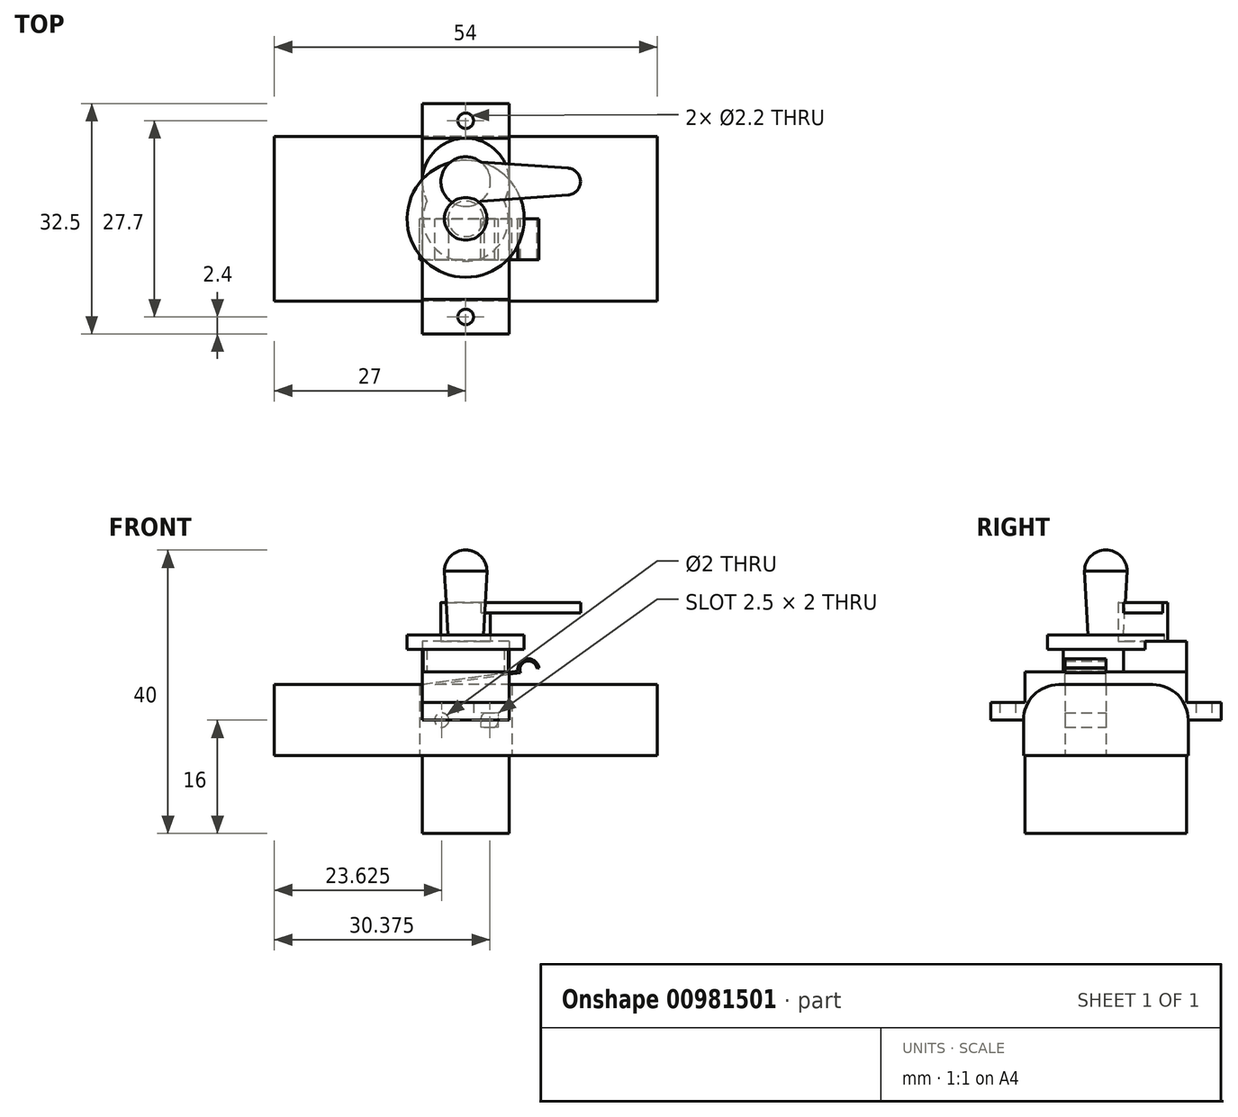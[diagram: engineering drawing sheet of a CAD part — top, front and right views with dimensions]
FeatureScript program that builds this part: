
annotation { "Feature Type Name" : "Feature", "Feature Type Description" : "" }
export const myFeature = defineFeature(function(context is Context, id is Id, definition is map)
    precondition{}
    {
        {
            var Q0;
            Q0=qCreatedBy(makeId("Right.planeOp"),FACE);
            var sketch = newSketch(context, id + "F0", { "sketchPlane" : qUnion([Q0])});
            skLineSegment(sketch, "E0.bottom", {"start": v(6.62, 5) * mm, "end": v(-6.63, 5) * mm});
            skLineSegment(sketch, "E0.top", {"start": v(11.63, -5) * mm, "end": v(-11.62, -5) * mm});
            skLineSegment(sketch, "E0.left", {"start": v(11.62, 0) * mm, "end": v(11.63, -5) * mm});
            skLineSegment(sketch, "E0.right", {"start": v(-11.63, 0) * mm, "end": v(-11.62, -5) * mm});
            skPoint(sketch, "E0.middle", {"position": v(0, 0) * mm});
            skPoint(sketch, "E1.visualSharp", {"position": v(-11.63, 5) * mm});
            skArc(sketch, "E1.filletArc", {"start": v(-6.63, 5) * mm, "mid": v(-10.16, 3.54) * mm, "end": v(-11.63, 0) * mm});
            skPoint(sketch, "E2.visualSharp", {"position": v(11.62, 5) * mm});
            skArc(sketch, "E2.filletArc", {"start": v(11.62, 0) * mm, "mid": v(10.16, 3.54) * mm, "end": v(6.62, 5) * mm});
            skSolve(sketch);
        }
        {
            var Q0;
            Q0 = qSketchRegion(id + "F0", true);
            extrude(context, id + "F1", {"entities" : qUnion([Q0]), "endBound" : BoundingType.SYMMETRIC, "depth" : 54 * mm, "offsetDistance" : 25 * mm});
        }
        {
            var Q0;
            Q0=qCreatedBy(makeId("Front.planeOp"),FACE);
            var sketch = newSketch(context, id + "F2", { "sketchPlane" : qUnion([Q0])});
            skLineSegment(sketch, "E3", {"start": v(0, 0) * mm, "end": v(0, 24) * mm});
            skArc(sketch, "E4", {"start": v(0, 24) * mm, "mid": v(2.12, 23.12) * mm, "end": v(3, 21) * mm});
            skLineSegment(sketch, "E5", {"start": v(3, 21) * mm, "end": v(2.5, 12) * mm});
            skLineSegment(sketch, "E6", {"start": v(2.5, 12) * mm, "end": v(6, 12) * mm});
            skLineSegment(sketch, "E7", {"start": v(6, 12) * mm, "end": v(6, 0) * mm});
            skLineSegment(sketch, "E8", {"start": v(0, 0) * mm, "end": v(6, 0) * mm});
            skSolve(sketch);
        }
        {
            var Q0;
            Q0 = qSketchRegion(id + "F2", true);
            var Q1;
            Q1=sQuery(id+"F2.wireOp",EDGE,"E3");
            revolve(context, id + "F3", {"surfaceOperationType" : NewSurfaceOperationType.NEW, "entities" : qUnion([Q0]), "axis" : qUnion([Q1]), "revolveType" : RevolveType.FULL});
        }
        {
            var Q0;
            Q0=makeQuery(id+"F3.opRevolve","SWEPT_FACE",FACE,{"disambiguationData":[OSD([sQuery(id+"F2.wireOp",EDGE,"E8")])]});
            var sketch = newSketch(context, id + "F4", { "sketchPlane" : qUnion([Q0])});
            skLineSegment(sketch, "E9.bottom", {"start": v(-5.75, 6.5) * mm, "end": v(5.75, 6.5) * mm});
            skLineSegment(sketch, "E9.top", {"start": v(-5.75, -6.5) * mm, "end": v(5.75, -6.5) * mm});
            skLineSegment(sketch, "E9.left", {"start": v(-5.75, 6.5) * mm, "end": v(-5.75, -6.5) * mm});
            skLineSegment(sketch, "E9.right", {"start": v(5.75, 6.5) * mm, "end": v(5.75, -6.5) * mm});
            skPoint(sketch, "E9.middle", {"position": v(0, 0) * mm});
            skSolve(sketch);
        }
        {
            var Q0;
            Q0 = qSketchRegion(id + "F4", true);
            extrude(context, id + "F5", {"entities" : qUnion([Q0]), "operationType" : NewBodyOperationType.ADD, "depth" : 13 * mm, "offsetDistance" : 25 * mm});
        }
        {
            var Q0;
            Q0=makeQuery(id+"F3.opRevolve","SWEPT_FACE",FACE,{"disambiguationData":[OSD([sQuery(id+"F2.wireOp",EDGE,"E6")])]});
            var sketch = newSketch(context, id + "F6", { "sketchPlane" : qUnion([Q0])});
            skCircle(sketch, "E10.cCircle", {"center": v(0, 0) * mm, "radius": 8.26 * mm});
            skLineSegment(sketch, "E10.0", {"start": v(8.26, 0) * mm, "end": v(4.13, -7.15) * mm, "construction": true});
            skLineSegment(sketch, "E10.1", {"start": v(4.13, -7.15) * mm, "end": v(-4.13, -7.15) * mm, "construction": true});
            skLineSegment(sketch, "E10.2", {"start": v(-4.13, -7.15) * mm, "end": v(-8.26, 0) * mm, "construction": true});
            skLineSegment(sketch, "E10.3", {"start": v(-8.26, 0) * mm, "end": v(-4.13, 7.15) * mm, "construction": true});
            skLineSegment(sketch, "E10.4", {"start": v(-4.13, 7.15) * mm, "end": v(4.13, 7.15) * mm, "construction": true});
            skLineSegment(sketch, "E10.5", {"start": v(4.13, 7.15) * mm, "end": v(8.26, 0) * mm, "construction": true});
            skSolve(sketch);
        }
        {
            var Q0;
            Q0 = qSketchRegion(id + "F6", true);
            var Q1;
            Q1 = qConstructionFilter(qBodyType(qCreatedBy(id + "F6" ,EDGE), BodyType.WIRE), ConstructionObject.NO);
            extrude(context, id + "F7", {"entities" : qUnion([Q0]), "operationType" : NewBodyOperationType.ADD, "surfaceOperationType" : NewSurfaceOperationType.ADD, "surfaceEntities" : qUnion([Q1]), "oppositeDirection" : true, "depth" : 2 * mm, "offsetDistance" : 25 * mm});
        }
        {
            var Q0;
            Q0=qCreatedBy(makeId("Top.planeOp"),FACE);
            var sketch = newSketch(context, id + "F8", { "sketchPlane" : qUnion([Q0])});
            skLineSegment(sketch, "E11.bottom", {"start": v(6.13, -11.38) * mm, "end": v(-6.12, -11.38) * mm});
            skLineSegment(sketch, "E11.top", {"start": v(6.12, 11.38) * mm, "end": v(-6.13, 11.38) * mm});
            skLineSegment(sketch, "E11.left", {"start": v(6.13, -11.38) * mm, "end": v(6.12, 11.38) * mm});
            skLineSegment(sketch, "E11.right", {"start": v(-6.12, -11.38) * mm, "end": v(-6.13, 11.37) * mm});
            skPoint(sketch, "E11.middle", {"position": v(0, 0) * mm});
            skSolve(sketch);
        }
        {
            var Q0;
            Q0 = qSketchRegion(id + "F8", true);
            extrude(context, id + "F9", {"entities" : qUnion([Q0]), "oppositeDirection" : true, "depth" : 16 * mm, "offsetDistance" : 25 * mm});
        }
        {
            var Q0;
            Q0=makeQuery(id+"F9.opExtrude","CAP_FACE",FACE,{"disambiguationData":[OSD([sQuery(id+"F8.wireOp",EDGE,"E11.bottom"),sQuery(id+"F8.wireOp",EDGE,"E11.top"),sQuery(id+"F8.wireOp",EDGE,"E11.left"),sQuery(id+"F8.wireOp",EDGE,"E11.right")])],"isStart":true});
            var sketch = newSketch(context, id + "F10", { "sketchPlane" : qUnion([Q0])});
            skLineSegment(sketch, "E12.bottom", {"start": v(6.13, -16.25) * mm, "end": v(-6.13, -16.25) * mm});
            skLineSegment(sketch, "E12.top", {"start": v(6.13, 16.25) * mm, "end": v(-6.13, 16.25) * mm});
            skLineSegment(sketch, "E12.left", {"start": v(6.13, -16.25) * mm, "end": v(6.13, 16.25) * mm});
            skLineSegment(sketch, "E12.right", {"start": v(-6.13, -16.25) * mm, "end": v(-6.13, 16.25) * mm});
            skPoint(sketch, "E12.middle", {"position": v(0, 0) * mm});
            skCircle(sketch, "E13", {"center": v(0, 13.85) * mm, "radius": 1.1 * mm});
            skCircle(sketch, "E14", {"center": v(0, -13.85) * mm, "radius": 1.1 * mm});
            skSolve(sketch);
        }
        {
            var Q0;
            Q0 = qSketchRegion(id + "F10", true);
            extrude(context, id + "F11", {"entities" : qUnion([Q0]), "operationType" : NewBodyOperationType.ADD, "depth" : 2.5 * mm, "offsetDistance" : 25 * mm});
        }
        {
            var Q0;
            Q0=makeQuery(id+"F11.opExtrude","CAP_FACE",FACE,{"disambiguationData":[OSD([sQuery(id+"F10.wireOp",EDGE,"E12.bottom"),sQuery(id+"F10.wireOp",EDGE,"E12.top"),sQuery(id+"F10.wireOp",EDGE,"E12.left"),sQuery(id+"F10.wireOp",EDGE,"E12.right"),sQuery(id+"F10.wireOp",EDGE,"E13"),sQuery(id+"F10.wireOp",EDGE,"E14")])],"isStart":false});
            var sketch = newSketch(context, id + "F12", { "sketchPlane" : qUnion([Q0])});
            skLineSegment(sketch, "E15.bottom", {"start": v(-6.13, 11.38) * mm, "end": v(6.13, 11.38) * mm});
            skLineSegment(sketch, "E15.top", {"start": v(-6.13, -11.38) * mm, "end": v(6.13, -11.38) * mm});
            skLineSegment(sketch, "E15.left", {"start": v(-6.13, 11.38) * mm, "end": v(-6.13, -11.38) * mm});
            skLineSegment(sketch, "E15.right", {"start": v(6.13, 11.38) * mm, "end": v(6.13, -11.38) * mm});
            skPoint(sketch, "E15.middle", {"position": v(0, 0) * mm});
            skSolve(sketch);
        }
        {
            var Q0;
            Q0 = qSketchRegion(id + "F12", true);
            extrude(context, id + "F13", {"entities" : qUnion([Q0]), "operationType" : NewBodyOperationType.ADD, "depth" : 4.3 * mm, "offsetDistance" : 25 * mm});
        }
        {
            var Q0;
            Q0=makeQuery(id+"F13.opExtrude","CAP_FACE",FACE,{"disambiguationData":[OSD([sQuery(id+"F12.wireOp",EDGE,"E15.bottom"),sQuery(id+"F12.wireOp",EDGE,"E15.top"),sQuery(id+"F12.wireOp",EDGE,"E15.left"),sQuery(id+"F12.wireOp",EDGE,"E15.right")])],"isStart":false});
            var sketch = newSketch(context, id + "F14", { "sketchPlane" : qUnion([Q0])});
            skArc(sketch, "E16", {"start": v(2.74, -0.23) * mm, "mid": v(0, 11.38) * mm, "end": v(-2.74, -0.23) * mm});
            skArc(sketch, "E17", {"start": v(-2.74, -0.23) * mm, "mid": v(0, -3.22) * mm, "end": v(2.74, -0.23) * mm});
            skSolve(sketch);
        }
        {
            var Q0;
            Q0 = qSketchRegion(id + "F14", true);
            extrude(context, id + "F15", {"entities" : qUnion([Q0]), "operationType" : NewBodyOperationType.ADD, "depth" : 4.3 * mm, "offsetDistance" : 25 * mm});
        }
        {
            var Q0;
            Q0=makeQuery(id+"F15.opExtrude","CAP_FACE",FACE,{"disambiguationData":[OSD([sQuery(id+"F14.wireOp",EDGE,"E16"),sQuery(id+"F14.wireOp",EDGE,"E17")])],"isStart":false});
            var sketch = newSketch(context, id + "F16", { "sketchPlane" : qUnion([Q0])});
            skCircle(sketch, "E18", {"center": v(0, 5.25) * mm, "radius": 3.5 * mm});
            skSolve(sketch);
        }
        {
            var Q0;
            Q0 = qSketchRegion(id + "F16", true);
            extrude(context, id + "F17", {"entities" : qUnion([Q0]), "depth" : 5.5 * mm, "offsetDistance" : 25 * mm});
        }
        {
            var Q0;
            Q0=makeQuery(id+"F17.opExtrude","CAP_FACE",FACE,{"disambiguationData":[OSD([sQuery(id+"F16.wireOp",EDGE,"E18")])],"isStart":false});
            var sketch = newSketch(context, id + "F18", { "sketchPlane" : qUnion([Q0])});
            skArc(sketch, "E19", {"start": v(14.43, 7.15) * mm, "mid": v(16.2, 5.25) * mm, "end": v(14.43, 3.35) * mm});
            skPoint(sketch, "E20", {"position": v(0, 5.25) * mm});
            skLineSegment(sketch, "E21", {"start": v(14.43, 3.35) * mm, "end": v(2.17, 2.5) * mm});
            skLineSegment(sketch, "E22", {"start": v(14.43, 7.15) * mm, "end": v(2.17, 8) * mm});
            skLineSegment(sketch, "E23", {"start": v(0, 5.25) * mm, "end": v(14.3, 5.25) * mm, "construction": true});
            skPoint(sketch, "E24", {"position": v(16.2, 5.25) * mm});
            skPoint(sketch, "E25", {"position": v(-3.5, 5.25) * mm});
            skPoint(sketch, "E25.positionSnap0", {"position": v(7.15, 5.25) * mm});
            skLineSegment(sketch, "E26", {"start": v(2.17, 2.5) * mm, "end": v(2.17, 8) * mm});
            skSolve(sketch);
        }
        {
            var Q0;
            Q0 = qSketchRegion(id + "F18", true);
            extrude(context, id + "F19", {"entities" : qUnion([Q0]), "operationType" : NewBodyOperationType.ADD, "oppositeDirection" : true, "depth" : 1.5 * mm, "offsetDistance" : 25 * mm});
        }
        {
            var Q0;
            Q0=qCreatedBy(makeId("Front.planeOp"),FACE);
            var sketch = newSketch(context, id + "F20", { "sketchPlane" : qUnion([Q0])});
            skLineSegment(sketch, "E27.bottom", {"start": v(6.5, 5) * mm, "end": v(-6.5, 5) * mm});
            skLineSegment(sketch, "E27.top", {"start": v(6.5, -5) * mm, "end": v(-6.5, -5) * mm});
            skLineSegment(sketch, "E27.left", {"start": v(6.5, 5) * mm, "end": v(6.5, -5) * mm});
            skLineSegment(sketch, "E27.right", {"start": v(-6.5, 5) * mm, "end": v(-6.5, -5) * mm});
            skPoint(sketch, "E27.middle", {"position": v(0, 0) * mm});
            skCircle(sketch, "E28", {"center": v(-3.38, 0) * mm, "radius": 1 * mm});
            skArc(sketch, "E29", {"start": v(2.62, 1) * mm, "mid": v(2.12, 0) * mm, "end": v(2.62, -1) * mm});
            skLineSegment(sketch, "E30", {"start": v(2.62, 1) * mm, "end": v(4.12, 1) * mm});
            skLineSegment(sketch, "E31", {"start": v(2.62, -1) * mm, "end": v(4.13, -1) * mm});
            skPoint(sketch, "E32.orphan", {"position": v(-3.38, -1) * mm});
            skPoint(sketch, "E33.orphan", {"position": v(-3.38, 1) * mm});
            skArc(sketch, "E34.trimOffspring", {"start": v(4.13, -1) * mm, "mid": v(4.63, 0) * mm, "end": v(4.12, 1) * mm});
            skLineSegment(sketch, "E35", {"start": v(-6.5, 5) * mm, "end": v(7.37, 6.94) * mm});
            skArc(sketch, "E36", {"start": v(7.37, 6.94) * mm, "mid": v(8.64, 8.63) * mm, "end": v(10.34, 7.35) * mm});
            skLineSegment(sketch, "E37", {"start": v(7.37, 6.94) * mm, "end": v(10.34, 7.35) * mm, "construction": true});
            skLineSegment(sketch, "E38.0", {"start": v(-4.33, 5) * mm, "end": v(7.74, 6.69) * mm});
            skArc(sketch, "E39.0", {"start": v(7.74, 6.69) * mm, "mid": v(8.54, 8.3) * mm, "end": v(10.04, 7.31) * mm});
            skLineSegment(sketch, "E40", {"start": v(10.04, 7.31) * mm, "end": v(10.34, 7.35) * mm});
            skSolve(sketch);
        }
        {
            var Q0;
            Q0 = qSketchRegion(id + "F20", true);
            extrude(context, id + "F21", {"entities" : qUnion([Q0]), "depth" : 5.75 * mm, "offsetDistance" : 25 * mm});
        }
    });
